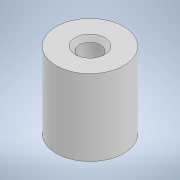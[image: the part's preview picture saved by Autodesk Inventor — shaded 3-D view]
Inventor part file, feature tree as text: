
AUTODESK INVENTOR PART (.ipt)
format: ipt  version: 2020 (Build 240168000, 168)  size: 101,376 bytes
history: native  units: mm
features: extrude x1, chamfer x1, sketch x1
ambient origin geometry x8: Origin, YZ Plane, XZ Plane, XY Plane, X Axis, Y Axis, Z Axis, Center Point
bodies: Solid1 (feature_tree)
feature tree (3):
  extrude  "Extrusion1"  Depth=9.0mm
  chamfer  "Chamfer1"  Distance=9.0mm
  sketch  "Sketch1"  dims[d0=2.5mm d1=8.0mm d2=9.0mm d3=0.0mm d4=0.5mm d5=2.0mm d6=45.0deg]
